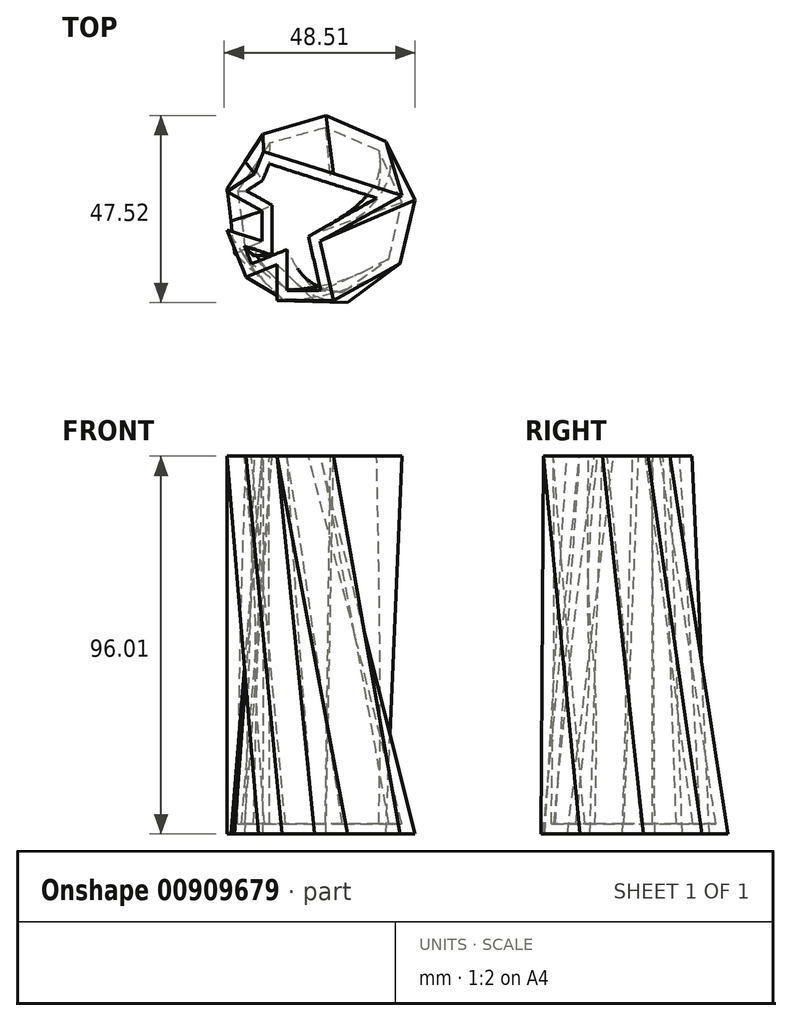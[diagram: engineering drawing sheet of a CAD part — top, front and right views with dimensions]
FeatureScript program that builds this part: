
annotation { "Feature Type Name" : "Feature", "Feature Type Description" : "" }
export const myFeature = defineFeature(function(context is Context, id is Id, definition is map)
    precondition{}
    {
        {
            var Q0;
            Q0=qCreatedBy(makeId("Top.planeOp"),FACE);
            var sketch = newSketch(context, id + "F0", { "sketchPlane" : qUnion([Q0])});
            skCircle(sketch, "E0.cCircle", {"center": v(0, 0) * mm, "radius": 22.82 * mm, "construction": true});
            skLineSegment(sketch, "E0.0", {"start": v(-23.61, 5.65) * mm, "end": v(-14.46, 19.5) * mm});
            skLineSegment(sketch, "E0.1", {"start": v(-14.46, 19.5) * mm, "end": v(1.47, 24.24) * mm});
            skLineSegment(sketch, "E0.2", {"start": v(1.47, 24.24) * mm, "end": v(16.7, 17.62) * mm});
            skLineSegment(sketch, "E0.3", {"start": v(16.7, 17.62) * mm, "end": v(24.12, 2.76) * mm});
            skLineSegment(sketch, "E0.4", {"start": v(24.12, 2.76) * mm, "end": v(20.26, -13.39) * mm});
            skLineSegment(sketch, "E0.5", {"start": v(20.26, -13.39) * mm, "end": v(6.91, -23.28) * mm});
            skLineSegment(sketch, "E0.6", {"start": v(6.91, -23.28) * mm, "end": v(-9.67, -22.27) * mm});
            skLineSegment(sketch, "E0.7", {"start": v(-9.67, -22.27) * mm, "end": v(-21.72, -10.85) * mm});
            skLineSegment(sketch, "E0.8", {"start": v(-21.72, -10.85) * mm, "end": v(-23.61, 5.65) * mm});
            skPoint(sketch, "E0.0.midPoint", {"position": v(-19.03, 12.58) * mm});
            skSolve(sketch);
        }
        {
            var Q0;
            Q0=makeQuery(id+"F0.imprint","IMPRINT",FACE,{"disambiguationData":[TD([[makeQuery(id+"F0.imprint","IMPRINT",EDGE,{"derivedFrom":sQuery(id+"F0.wireOp",EDGE,"E0.0")}),-1.0]])]});
            cPlane(context, id + "F1", {"entities" : qUnion([Q0]), "cplaneType" : CPlaneType.OFFSET, "offset" : 96.01 * mm, "width" : 152.4 * mm, "height" : 152.4 * mm});
        }
        {
            var Q0;
            Q0=qCreatedBy(id+"F1.planeOp",FACE);
            var sketch = newSketch(context, id + "F2", { "sketchPlane" : qUnion([Q0])});
            skLineSegment(sketch, "E1", {"start": v(-14.38, 15.08) * mm, "end": v(3.4, 9.44) * mm});
            skLineSegment(sketch, "E2", {"start": v(3.4, 9.44) * mm, "end": v(20.78, 3.93) * mm});
            skLineSegment(sketch, "E3", {"start": v(20.78, 3.93) * mm, "end": v(0, -7.7) * mm});
            skLineSegment(sketch, "E4", {"start": v(0, -7.7) * mm, "end": v(3.4, -22.7) * mm});
            skLineSegment(sketch, "E5", {"start": v(3.4, -22.7) * mm, "end": v(-10.97, -22.7) * mm});
            skLineSegment(sketch, "E6", {"start": v(-10.97, -22.7) * mm, "end": v(-10.97, -13.58) * mm});
            skLineSegment(sketch, "E7", {"start": v(-10.97, -13.58) * mm, "end": v(-18.84, -16.76) * mm});
            skLineSegment(sketch, "E8", {"start": v(-18.84, -16.76) * mm, "end": v(-23.63, -4.9) * mm});
            skLineSegment(sketch, "E9", {"start": v(-23.63, -4.9) * mm, "end": v(-14.78, -7.7) * mm});
            skLineSegment(sketch, "E10", {"start": v(-14.78, -7.7) * mm, "end": v(-14.78, 0) * mm});
            skLineSegment(sketch, "E11", {"start": v(-14.78, 0) * mm, "end": v(-23.63, 4.93) * mm});
            skLineSegment(sketch, "E12", {"start": v(-23.63, 4.93) * mm, "end": v(-16.7, 9.44) * mm});
            skLineSegment(sketch, "E13", {"start": v(-16.7, 9.44) * mm, "end": v(-14.38, 15.08) * mm});
            skSolve(sketch);
        }
        {
            var Q0;
            Q0=makeQuery(id+"F0.imprint","IMPRINT",FACE,{"disambiguationData":[TD([[makeQuery(id+"F0.imprint","IMPRINT",EDGE,{"derivedFrom":sQuery(id+"F0.wireOp",EDGE,"E0.0")}),-1.0]])]});
            var Q1;
            Q1=makeQuery(id+"F2.imprint","IMPRINT",FACE,{"disambiguationData":[TD([[makeQuery(id+"F2.imprint","IMPRINT",EDGE,{"derivedFrom":sQuery(id+"F2.wireOp",EDGE,"E1")}),-1.0]])]});
            loft(context, id + "F3", {"sheetProfilesArray" : [{ "sheetProfileEntities" : qUnion([Q0]) }, { "sheetProfileEntities" : qUnion([Q1]) }]});
        }
        {
            var Q0;
            Q0=makeQuery(id+"F3.opLoft","CAP_FACE",FACE,{"disambiguationData":[OSD([makeQuery(id+"F2.imprint","IMPRINT",FACE,{"disambiguationData":[TD([[makeQuery(id+"F2.imprint","IMPRINT",EDGE,{"derivedFrom":sQuery(id+"F2.wireOp",EDGE,"E1")}),-1.0]])]})])],"isStart":true});
            shell(context, id + "F4", {"entities" : qUnion([Q0]), "thickness" : 2.54 * mm});
        }
    });
